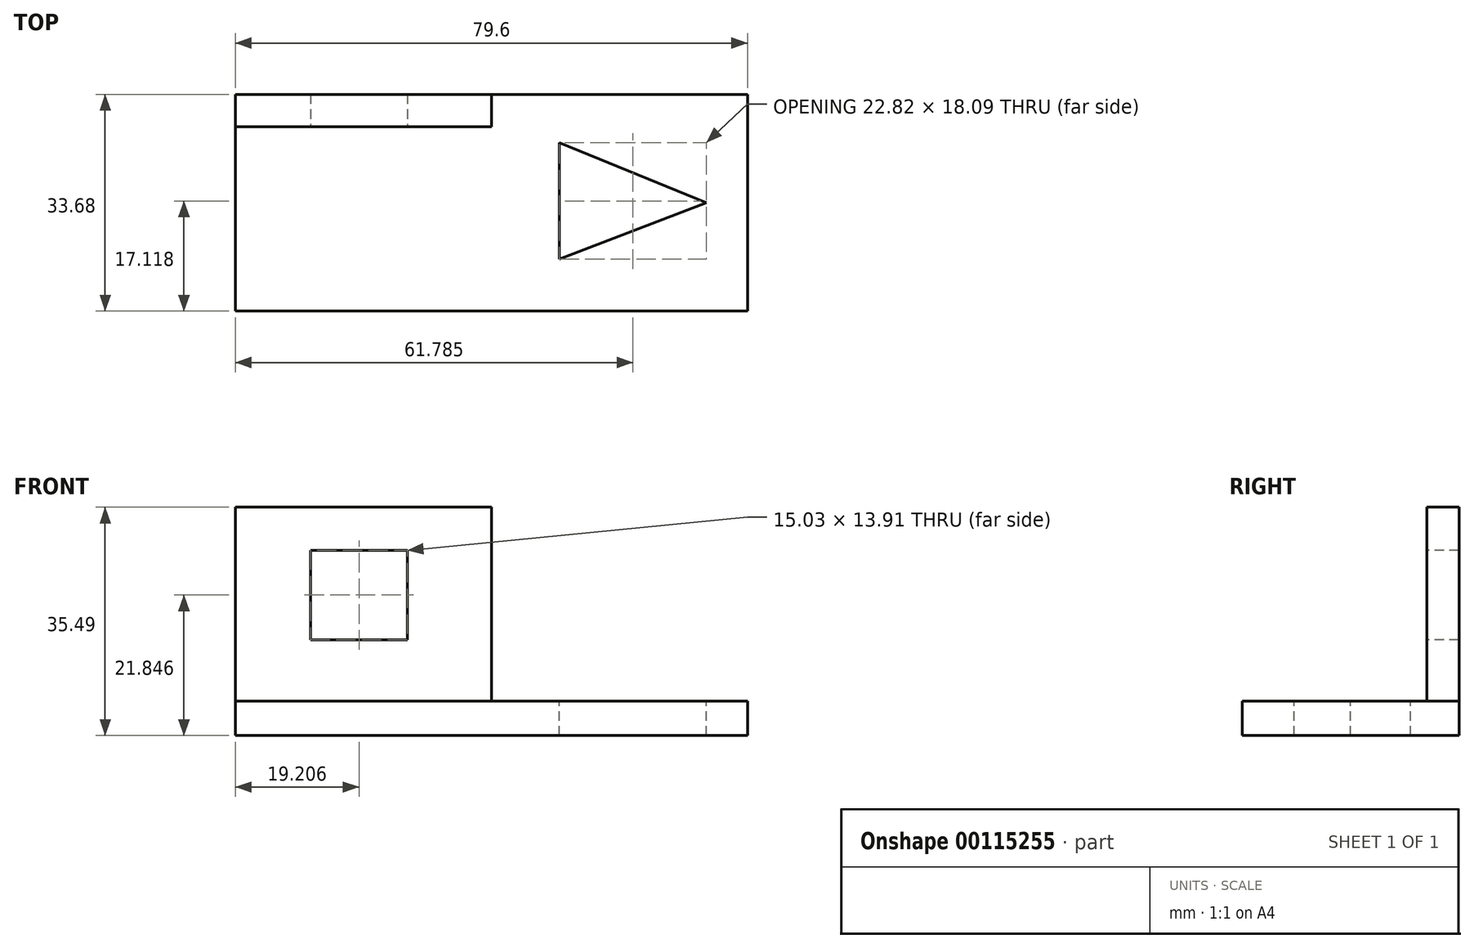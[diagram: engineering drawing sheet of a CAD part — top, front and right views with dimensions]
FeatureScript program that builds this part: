
annotation { "Feature Type Name" : "Feature", "Feature Type Description" : "" }
export const myFeature = defineFeature(function(context is Context, id is Id, definition is map)
    precondition{}
    {
        {
            var Q0;
            Q0=qCreatedBy(makeId("Top.planeOp"),FACE);
            var sketch = newSketch(context, id + "F0", { "sketchPlane" : qUnion([Q0])});
            skLineSegment(sketch, "E0.bottom", {"start": v(-39.8, 16.84) * mm, "end": v(39.8, 16.84) * mm});
            skLineSegment(sketch, "E0.top", {"start": v(-39.8, -16.84) * mm, "end": v(39.8, -16.84) * mm});
            skLineSegment(sketch, "E0.left", {"start": v(-39.8, 16.84) * mm, "end": v(-39.8, -16.84) * mm});
            skLineSegment(sketch, "E0.right", {"start": v(39.8, 16.84) * mm, "end": v(39.8, -16.84) * mm});
            skPoint(sketch, "E0.middle", {"position": v(0, 0) * mm});
            skSolve(sketch);
        }
        {
            var Q0;
            Q0=makeQuery(id+"F0.imprint","IMPRINT",FACE,{"disambiguationData":[TD([[makeQuery(id+"F0.imprint","IMPRINT",EDGE,{"derivedFrom":sQuery(id+"F0.wireOp",EDGE,"E0.bottom")}),-1.0]])]});
            extrude(context, id + "F1", {"entities" : qUnion([Q0]), "depth" : 5.36 * mm});
        }
        {
            var Q0;
            Q0=makeQuery(id+"F1.opExtrude","CAP_FACE",FACE,{"disambiguationData":[OSD([sQuery(id+"F0.wireOp",EDGE,"E0.bottom"),sQuery(id+"F0.wireOp",EDGE,"E0.top"),sQuery(id+"F0.wireOp",EDGE,"E0.left"),sQuery(id+"F0.wireOp",EDGE,"E0.right")])],"isStart":false});
            var sketch = newSketch(context, id + "F2", { "sketchPlane" : qUnion([Q0])});
            skLineSegment(sketch, "E1.bottom", {"start": v(-39.8, 16.84) * mm, "end": v(0, 16.84) * mm});
            skLineSegment(sketch, "E1.top", {"start": v(-39.8, 11.83) * mm, "end": v(0, 11.83) * mm});
            skLineSegment(sketch, "E1.left", {"start": v(-39.8, 16.84) * mm, "end": v(-39.8, 11.83) * mm});
            skLineSegment(sketch, "E1.right", {"start": v(0, 16.84) * mm, "end": v(0, 11.83) * mm});
            skSolve(sketch);
        }
        {
            var Q0;
            Q0 = qSketchRegion(id + "F2", true);
            extrude(context, id + "F3", {"entities" : qUnion([Q0]), "operationType" : NewBodyOperationType.ADD, "depth" : 30.13 * mm});
        }
        {
            var Q0;
            Q0=makeQuery(id+"F3.opExtrude","SWEPT_FACE",FACE,{"disambiguationData":[OSD([sQuery(id+"F2.wireOp",EDGE,"E1.top")])]});
            var sketch = newSketch(context, id + "F4", { "sketchPlane" : qUnion([Q0])});
            skLineSegment(sketch, "E2.bottom", {"start": v(-28.1, 28.8) * mm, "end": v(-13.08, 28.8) * mm});
            skLineSegment(sketch, "E2.top", {"start": v(-28.1, 14.89) * mm, "end": v(-13.08, 14.89) * mm});
            skLineSegment(sketch, "E2.left", {"start": v(-28.1, 28.8) * mm, "end": v(-28.1, 14.89) * mm});
            skLineSegment(sketch, "E2.right", {"start": v(-13.08, 28.8) * mm, "end": v(-13.08, 14.89) * mm});
            skPoint(sketch, "E2.middle", {"position": v(-20.6, 21.85) * mm});
            skSolve(sketch);
        }
        {
            var Q0;
            Q0 = qSketchRegion(id + "F4", true);
            extrude(context, id + "F5", {"entities" : qUnion([Q0]), "operationType" : NewBodyOperationType.REMOVE, "endBound" : BoundingType.THROUGH_ALL, "oppositeDirection" : true, "depth" : 25.4 * mm});
        }
        {
            var Q0;
            Q0=makeQuery(id+"F1.opExtrude","CAP_FACE",FACE,{"disambiguationData":[OSD([sQuery(id+"F0.wireOp",EDGE,"E0.bottom"),sQuery(id+"F0.wireOp",EDGE,"E0.top"),sQuery(id+"F0.wireOp",EDGE,"E0.left"),sQuery(id+"F0.wireOp",EDGE,"E0.right")])],"isStart":false});
            var sketch = newSketch(context, id + "F6", { "sketchPlane" : qUnion([Q0])});
            skLineSegment(sketch, "E3", {"start": v(10.58, 9.32) * mm, "end": v(10.58, -8.77) * mm});
            skLineSegment(sketch, "E4", {"start": v(10.58, -8.77) * mm, "end": v(33.4, 0) * mm});
            skLineSegment(sketch, "E5", {"start": v(33.4, 0) * mm, "end": v(10.58, 9.32) * mm});
            skSolve(sketch);
        }
        {
            var Q0;
            Q0 = qSketchRegion(id + "F6", true);
            extrude(context, id + "F7", {"entities" : qUnion([Q0]), "operationType" : NewBodyOperationType.REMOVE, "endBound" : BoundingType.THROUGH_ALL, "oppositeDirection" : true, "depth" : 25.4 * mm});
        }
    });
